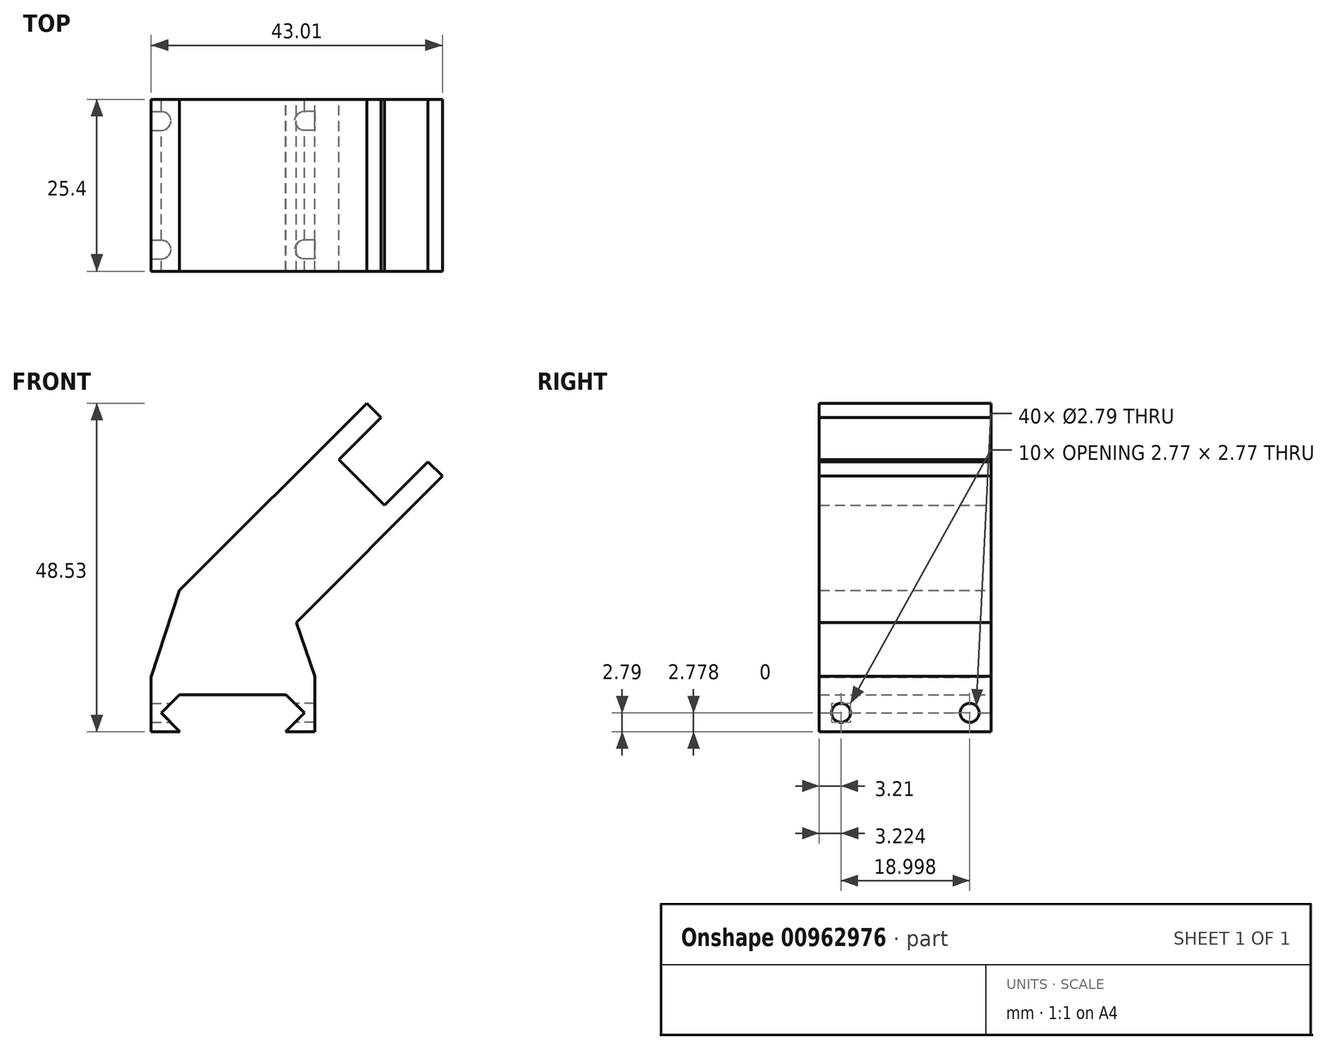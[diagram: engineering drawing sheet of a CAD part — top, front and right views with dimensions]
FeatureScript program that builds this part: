
annotation { "Feature Type Name" : "Feature", "Feature Type Description" : "" }
export const myFeature = defineFeature(function(context is Context, id is Id, definition is map)
    precondition{}
    {
        {
            var Q0;
            Q0=qCreatedBy(makeId("Front.planeOp"),FACE);
            var sketch = newSketch(context, id + "F0", { "sketchPlane" : qUnion([Q0])});
            skLineSegment(sketch, "E0", {"start": v(8.24, -9.31) * mm, "end": v(11, -6.54) * mm});
            skLineSegment(sketch, "E1", {"start": v(11, -6.54) * mm, "end": v(8.23, -3.78) * mm});
            skLineSegment(sketch, "E2.MirrorCS", {"start": v(-10.13, -6.54) * mm, "end": v(-7.35, -3.78) * mm});
            skLineSegment(sketch, "E3.MirrorCS", {"start": v(-7.36, -9.3) * mm, "end": v(-10.13, -6.54) * mm});
            skLineSegment(sketch, "E4.bottom", {"start": v(-7.36, -9.3) * mm, "end": v(-11.63, -9.3) * mm});
            skLineSegment(sketch, "E5.top", {"start": v(8.32, -3.86) * mm, "end": v(-7.44, -3.86) * mm});
            skLineSegment(sketch, "E6.right", {"start": v(-11.63, -1.23) * mm, "end": v(-11.63, -9.3) * mm});
            skLineSegment(sketch, "E7.top", {"start": v(12.55, -9.31) * mm, "end": v(8.24, -9.31) * mm});
            skLineSegment(sketch, "E7.left", {"start": v(12.55, -1.1) * mm, "end": v(12.55, -9.31) * mm});
            skLineSegment(sketch, "E8.right", {"start": v(-7.44, 11.55) * mm, "end": v(-7.44, 11.55) * mm});
            skLineSegment(sketch, "E9", {"start": v(9.8, 6.84) * mm, "end": v(12.55, -1.1) * mm});
            skLineSegment(sketch, "E10", {"start": v(-7.44, 11.55) * mm, "end": v(-11.63, -1.23) * mm});
            skLineSegment(sketch, "E11.top", {"start": v(16.07, 30.88) * mm, "end": v(22.8, 24.14) * mm});
            skLineSegment(sketch, "E11.left", {"start": v(-7.44, 11.55) * mm, "end": v(14.03, 33.02) * mm});
            skLineSegment(sketch, "E11.right", {"start": v(9.8, 6.84) * mm, "end": v(24.95, 22) * mm});
            skLineSegment(sketch, "E12.bottom", {"start": v(20.23, 39.22) * mm, "end": v(22.32, 37.13) * mm});
            skLineSegment(sketch, "E12.left", {"start": v(20.23, 39.22) * mm, "end": v(13.98, 32.97) * mm});
            skLineSegment(sketch, "E12.right", {"start": v(22.32, 37.13) * mm, "end": v(16.07, 30.88) * mm});
            skLineSegment(sketch, "E13.bottom", {"start": v(29.24, 30.58) * mm, "end": v(31.38, 28.44) * mm});
            skLineSegment(sketch, "E13.left", {"start": v(29.24, 30.58) * mm, "end": v(22.8, 24.14) * mm});
            skLineSegment(sketch, "E13.right", {"start": v(31.38, 28.44) * mm, "end": v(24.95, 22) * mm});
            skLineSegment(sketch, "E14.trimOffspring", {"start": v(-7.44, -1.2) * mm, "end": v(-7.44, -1.21) * mm});
            skPoint(sketch, "E15.top.end.orphan", {"position": v(-7.44, 8.88) * mm});
            skSolve(sketch);
        }
        {
            var Q0;
            {var subQ8=sQuery(id+"F0.wireOp",EDGE,"E8.right");Q0=makeQuery(id+"F0.imprint","IMPRINT",FACE,{"disambiguationData":[TD([[makeQuery(id+"F0.imprint","IMPRINT",EDGE,{"derivedFrom":subQ8}),1.0]])]});}
            var Q1;
            {var subQ6=sQuery(id+"F0.wireOp",EDGE,"E0");Q1=makeQuery(id+"F0.imprint","IMPRINT",FACE,{"disambiguationData":[TD([[makeQuery(id+"F0.imprint","IMPRINT",EDGE,{"derivedFrom":subQ6}),-1.0]])]});}
            var Q2;
            Q2=makeQuery(id+"F0.imprint","IMPRINT",FACE,{"disambiguationData":[TD([[makeQuery(id+"F0.imprint","IMPRINT",EDGE,{"derivedFrom":sQuery(id+"F0.wireOp",EDGE,"E12.bottom")}),-1.0]])]});
            var Q3;
            Q3=makeQuery(id+"F0.imprint","IMPRINT",FACE,{"disambiguationData":[TD([[makeQuery(id+"F0.imprint","IMPRINT",EDGE,{"derivedFrom":sQuery(id+"F0.wireOp",EDGE,"E13.bottom")}),-1.0]])]});
            extrude(context, id + "F1", {"entities" : qUnion([Q0, Q1, Q2, Q3]), "depth" : 25.4 * mm, "offsetDistance" : 25.4 * mm});
        }
        {
            var Q0;
            Q0=qCreatedBy(makeId("Right.planeOp"),FACE);
            var sketch = newSketch(context, id + "F2", { "sketchPlane" : qUnion([Q0])});
            skPoint(sketch, "E16", {"position": v(-22.19, -6.52) * mm});
            skPoint(sketch, "E17", {"position": v(-3.2, -6.52) * mm});
            skSolve(sketch);
        }
        {
            var Q0;
            Q0=sQuery(id+"F2.wireOp",VERTEX,"E16");
            var Q1;
            Q1=sQuery(id+"F2.wireOp",VERTEX,"E17");
            var Q2;
            Q2=makeQuery(id+"F1.opExtrude","SWEPT_BODY",BODY,{"disambiguationData":[OSD([sQuery(id+"F0.wireOp",EDGE,"E0"),sQuery(id+"F0.wireOp",EDGE,"E1"),sQuery(id+"F0.wireOp",EDGE,"E2.MirrorCS"),sQuery(id+"F0.wireOp",EDGE,"E3.MirrorCS"),sQuery(id+"F0.wireOp",EDGE,"E4.bottom"),sQuery(id+"F0.wireOp",EDGE,"E5.top"),sQuery(id+"F0.wireOp",EDGE,"E6.right"),sQuery(id+"F0.wireOp",EDGE,"E7.top"),sQuery(id+"F0.wireOp",EDGE,"E7.left"),sQuery(id+"F0.wireOp",EDGE,"E8.right"),sQuery(id+"F0.wireOp",EDGE,"E9"),sQuery(id+"F0.wireOp",EDGE,"E10"),sQuery(id+"F0.wireOp",EDGE,"E11.top"),sQuery(id+"F0.wireOp",EDGE,"E11.left"),sQuery(id+"F0.wireOp",EDGE,"E11.right"),sQuery(id+"F0.wireOp",EDGE,"E12.bottom"),sQuery(id+"F0.wireOp",EDGE,"E12.left"),sQuery(id+"F0.wireOp",EDGE,"E12.right"),sQuery(id+"F0.wireOp",EDGE,"E13.bottom"),sQuery(id+"F0.wireOp",EDGE,"E13.left"),sQuery(id+"F0.wireOp",EDGE,"E13.right"),sQuery(id+"F0.wireOp",EDGE,"E8.right")])]});
            hole(context, id + "F3", {"style" : HoleStyle.SIMPLE, "endStyle" : HoleEndStyle.BLIND, "oppositeDirection" : true, "holeDiameter" : 2.8 * mm, "majorDiameter" : 6.35 * mm, "holeDepth" : 25.4 * mm, "isTappedThrough" : true, "tappedDepth" : 12.7 * mm, "tapClearance" : 3, "locations" : qUnion([Q0, Q1]), "scope" : qUnion([Q2])});
        }
        {
            var Q0;
            Q0=sQuery(id+"F2.wireOp",VERTEX,"E17");
            var Q1;
            Q1=sQuery(id+"F2.wireOp",VERTEX,"E16");
            var Q2;
            Q2=makeQuery(id+"F1.opExtrude","SWEPT_BODY",BODY,{"disambiguationData":[OSD([sQuery(id+"F0.wireOp",EDGE,"E0"),sQuery(id+"F0.wireOp",EDGE,"E1"),sQuery(id+"F0.wireOp",EDGE,"E2.MirrorCS"),sQuery(id+"F0.wireOp",EDGE,"E3.MirrorCS"),sQuery(id+"F0.wireOp",EDGE,"E4.bottom"),sQuery(id+"F0.wireOp",EDGE,"E5.top"),sQuery(id+"F0.wireOp",EDGE,"E6.right"),sQuery(id+"F0.wireOp",EDGE,"E7.top"),sQuery(id+"F0.wireOp",EDGE,"E7.left"),sQuery(id+"F0.wireOp",EDGE,"E8.right"),sQuery(id+"F0.wireOp",EDGE,"E9"),sQuery(id+"F0.wireOp",EDGE,"E10"),sQuery(id+"F0.wireOp",EDGE,"E11.top"),sQuery(id+"F0.wireOp",EDGE,"E11.left"),sQuery(id+"F0.wireOp",EDGE,"E11.right"),sQuery(id+"F0.wireOp",EDGE,"E12.bottom"),sQuery(id+"F0.wireOp",EDGE,"E12.left"),sQuery(id+"F0.wireOp",EDGE,"E12.right"),sQuery(id+"F0.wireOp",EDGE,"E13.bottom"),sQuery(id+"F0.wireOp",EDGE,"E13.left"),sQuery(id+"F0.wireOp",EDGE,"E13.right"),sQuery(id+"F0.wireOp",EDGE,"E8.right")])]});
            hole(context, id + "F4", {"style" : HoleStyle.SIMPLE, "endStyle" : HoleEndStyle.BLIND, "holeDiameter" : 2.8 * mm, "majorDiameter" : 6.35 * mm, "holeDepth" : 25.4 * mm, "isTappedThrough" : true, "tappedDepth" : 12.7 * mm, "tapClearance" : 3, "locations" : qUnion([Q0, Q1]), "scope" : qUnion([Q2])});
        }
        {
            var Q0;
            Q0=makeQuery(id+"F1.opExtrude","SWEPT_BODY",BODY,{"disambiguationData":[OSD([sQuery(id+"F0.wireOp",EDGE,"E0"),sQuery(id+"F0.wireOp",EDGE,"E1"),sQuery(id+"F0.wireOp",EDGE,"E2.MirrorCS"),sQuery(id+"F0.wireOp",EDGE,"E3.MirrorCS"),sQuery(id+"F0.wireOp",EDGE,"E4.bottom"),sQuery(id+"F0.wireOp",EDGE,"E5.top"),sQuery(id+"F0.wireOp",EDGE,"E6.right"),sQuery(id+"F0.wireOp",EDGE,"E7.top"),sQuery(id+"F0.wireOp",EDGE,"E7.left"),sQuery(id+"F0.wireOp",EDGE,"E8.right"),sQuery(id+"F0.wireOp",EDGE,"E9"),sQuery(id+"F0.wireOp",EDGE,"E10"),sQuery(id+"F0.wireOp",EDGE,"E11.top"),sQuery(id+"F0.wireOp",EDGE,"E11.left"),sQuery(id+"F0.wireOp",EDGE,"E11.right"),sQuery(id+"F0.wireOp",EDGE,"E12.bottom"),sQuery(id+"F0.wireOp",EDGE,"E12.left"),sQuery(id+"F0.wireOp",EDGE,"E12.right"),sQuery(id+"F0.wireOp",EDGE,"E13.bottom"),sQuery(id+"F0.wireOp",EDGE,"E13.left"),sQuery(id+"F0.wireOp",EDGE,"E13.right"),sQuery(id+"F0.wireOp",EDGE,"E8.right")])]});
            transform(context, id + "F5", {"entities" : qUnion([Q0]), "transformType" : TransformType.TRANSLATION_3D, "dx" : 0 * mm, "dy" : 0 * mm, "dz" : 0 * mm, "makeCopy" : true});
        }
    });
